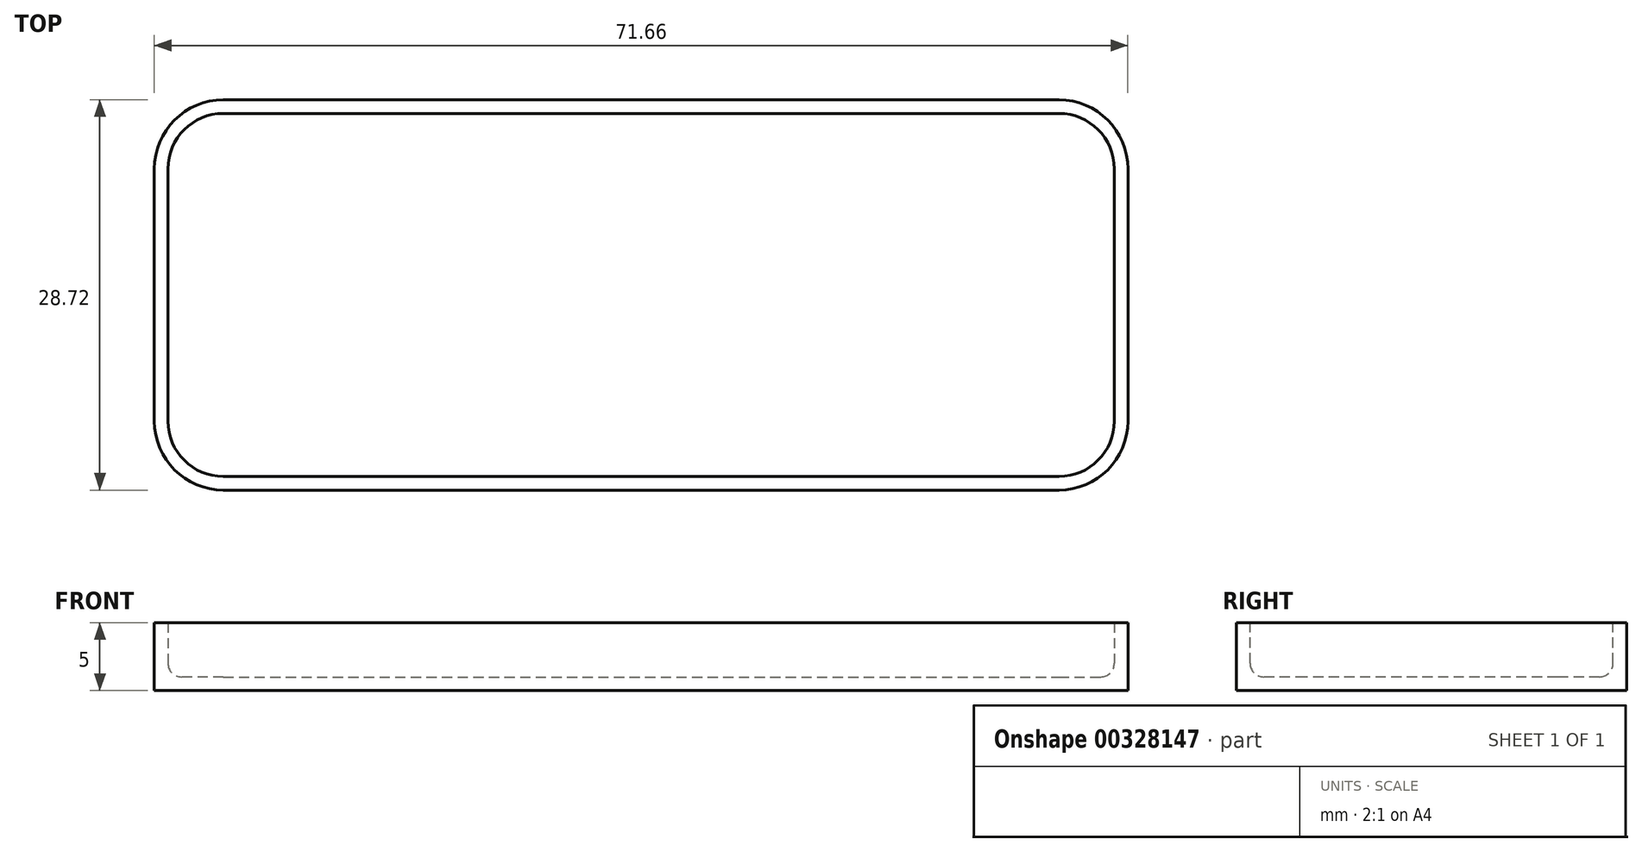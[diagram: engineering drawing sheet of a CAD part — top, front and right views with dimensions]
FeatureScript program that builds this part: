
annotation { "Feature Type Name" : "Feature", "Feature Type Description" : "" }
export const myFeature = defineFeature(function(context is Context, id is Id, definition is map)
    precondition{}
    {
        {
            var Q0;
            Q0=qCreatedBy(makeId("Top.planeOp"),FACE);
            var sketch = newSketch(context, id + "F0", { "sketchPlane" : qUnion([Q0])});
            skLineSegment(sketch, "E0.bottom", {"start": v(-54.33, 38.36) * mm, "end": v(17.33, 38.36) * mm});
            skLineSegment(sketch, "E0.top", {"start": v(-54.33, 9.64) * mm, "end": v(17.33, 9.64) * mm});
            skLineSegment(sketch, "E0.left", {"start": v(-54.33, 38.36) * mm, "end": v(-54.33, 9.64) * mm});
            skLineSegment(sketch, "E0.right", {"start": v(17.33, 38.36) * mm, "end": v(17.33, 9.64) * mm});
            skSolve(sketch);
        }
        {
            var Q0;
            Q0=makeQuery(id+"F0.imprint","IMPRINT",FACE,{"disambiguationData":[TD([[makeQuery(id+"F0.imprint","IMPRINT",EDGE,{"derivedFrom":sQuery(id+"F0.wireOp",EDGE,"E0.bottom")}),-1.0]])]});
            extrude(context, id + "F1", {"entities" : qUnion([Q0]), "depth" : 5 * mm});
        }
        {
            var Q0;
            Q0=makeQuery(id+"F1.opExtrude","SWEPT_EDGE",EDGE,{"disambiguationData":[OSD([sQuery(id+"F0.wireOp",EDGE,"E0.bottom"),sQuery(id+"F0.wireOp",EDGE,"E0.left")])]});
            fillet(context, id + "F2", {"entities" : qUnion([Q0]), "radius" : 5.08 * mm, "tangentPropagation" : true, "allowEdgeOverflow" : false});
        }
        {
            var Q0;
            Q0=makeQuery(id+"F1.opExtrude","SWEPT_EDGE",EDGE,{"disambiguationData":[OSD([sQuery(id+"F0.wireOp",EDGE,"E0.top"),sQuery(id+"F0.wireOp",EDGE,"E0.left")])]});
            fillet(context, id + "F3", {"entities" : qUnion([Q0]), "radius" : 5.08 * mm, "tangentPropagation" : true, "allowEdgeOverflow" : false});
        }
        {
            var Q0;
            Q0=makeQuery(id+"F1.opExtrude","SWEPT_EDGE",EDGE,{"disambiguationData":[OSD([sQuery(id+"F0.wireOp",EDGE,"E0.top"),sQuery(id+"F0.wireOp",EDGE,"E0.right")])]});
            fillet(context, id + "F4", {"entities" : qUnion([Q0]), "radius" : 5.08 * mm, "tangentPropagation" : true, "allowEdgeOverflow" : false});
        }
        {
            var Q0;
            Q0=makeQuery(id+"F1.opExtrude","SWEPT_EDGE",EDGE,{"disambiguationData":[OSD([sQuery(id+"F0.wireOp",EDGE,"E0.bottom"),sQuery(id+"F0.wireOp",EDGE,"E0.right")])]});
            fillet(context, id + "F5", {"entities" : qUnion([Q0]), "radius" : 5.08 * mm, "tangentPropagation" : true, "allowEdgeOverflow" : false});
        }
        {
            var Q0;
            Q0=makeQuery(id+"F1.opExtrude","CAP_FACE",FACE,{"disambiguationData":[OSD([sQuery(id+"F0.wireOp",EDGE,"E0.bottom"),sQuery(id+"F0.wireOp",EDGE,"E0.top"),sQuery(id+"F0.wireOp",EDGE,"E0.left"),sQuery(id+"F0.wireOp",EDGE,"E0.right")])],"isStart":false});
            shell(context, id + "F6", {"entities" : qUnion([Q0]), "thickness" : 1 * mm});
        }
        {
            var Q0;
            Q0=makeQuery(id+"F6.opShell","OFFSET_FACE",FACE,{"disambiguationData":[OSD([sQuery(id+"F0.wireOp",EDGE,"E0.bottom"),sQuery(id+"F0.wireOp",EDGE,"E0.top"),sQuery(id+"F0.wireOp",EDGE,"E0.left"),sQuery(id+"F0.wireOp",EDGE,"E0.right")])]});
            fillet(context, id + "F7", {"entities" : qUnion([Q0]), "radius" : 1 * mm, "tangentPropagation" : true, "allowEdgeOverflow" : false});
        }
    });
